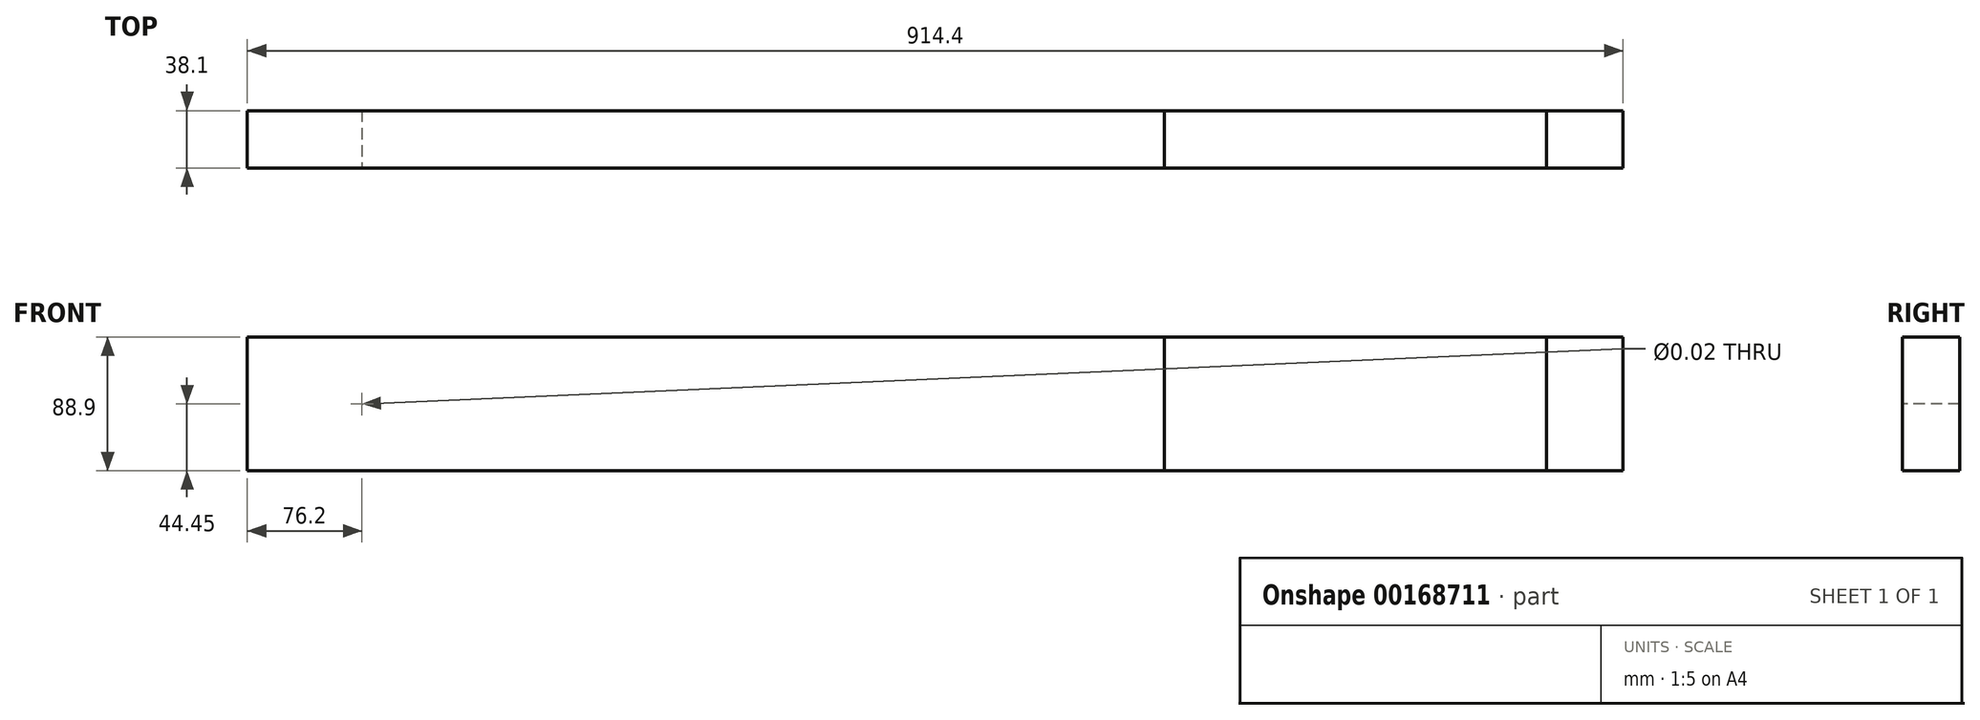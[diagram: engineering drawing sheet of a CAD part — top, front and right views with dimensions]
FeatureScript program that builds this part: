
annotation { "Feature Type Name" : "Feature", "Feature Type Description" : "" }
export const myFeature = defineFeature(function(context is Context, id is Id, definition is map)
    precondition{}
    {
        {
            var Q0;
            Q0=qCreatedBy(makeId("Right.planeOp"),FACE);
            var sketch = newSketch(context, id + "F0", { "sketchPlane" : qUnion([Q0])});
            skLineSegment(sketch, "E0.bottom", {"start": v(19.05, 44.45) * mm, "end": v(-19.05, 44.45) * mm});
            skLineSegment(sketch, "E0.top", {"start": v(19.05, -44.45) * mm, "end": v(-19.05, -44.45) * mm});
            skLineSegment(sketch, "E0.left", {"start": v(19.05, 44.45) * mm, "end": v(19.05, -44.45) * mm});
            skLineSegment(sketch, "E0.right", {"start": v(-19.05, 44.45) * mm, "end": v(-19.05, -44.45) * mm});
            skPoint(sketch, "E0.middle", {"position": v(0, 0) * mm});
            skSolve(sketch);
        }
        {
            var Q0;
            Q0=makeQuery(id+"F0.imprint","IMPRINT",FACE,{"disambiguationData":[TD([[makeQuery(id+"F0.imprint","IMPRINT",EDGE,{"derivedFrom":sQuery(id+"F0.wireOp",EDGE,"E0.bottom")}),1.0]])]});
            extrude(context, id + "F1", {"entities" : qUnion([Q0]), "depth" : 152.4 * mm});
        }
        {
            var Q0;
            Q0=makeQuery(id+"F1.opExtrude","SWEPT_FACE",FACE,{"disambiguationData":[OSD([sQuery(id+"F0.wireOp",EDGE,"E0.right")])]});
            var sketch = newSketch(context, id + "F2", { "sketchPlane" : qUnion([Q0])});
            skLineSegment(sketch, "E1", {"start": v(0, 0) * mm, "end": v(152.4, 0) * mm, "construction": true});
            skPoint(sketch, "E2", {"position": v(76.2, 0) * mm});
            skSolve(sketch);
        }
        {
            var Q0;
            Q0=sQuery(id+"F2.wireOp",VERTEX,"E2");
            var Q1;
            Q1=makeQuery(id+"F1.opExtrude","SWEPT_BODY",BODY,{"disambiguationData":[OSD([sQuery(id+"F0.wireOp",EDGE,"E0.bottom"),sQuery(id+"F0.wireOp",EDGE,"E0.top"),sQuery(id+"F0.wireOp",EDGE,"E0.left"),sQuery(id+"F0.wireOp",EDGE,"E0.right")])]});
            hole(context, id + "F3", {"style" : HoleStyle.SIMPLE, "endStyle" : HoleEndStyle.THROUGH, "standardTappedOrClearance" : lookupTablePath({ "standard" : "ANSI", "size" : "1/2 (0.5)", "type" : "Drilled" }), "standardBlindInLast" : lookupTablePath({ "standard" : "ANSI", "size" : "1/2", "type" : "Drilled" }), "holeDiameter" : 1 / 50.8 * mm, "locations" : qUnion([Q0]), "scope" : qUnion([Q1]), "isTappedThrough" : true});
        }
        {
            var Q0;
            Q0=makeQuery(id+"F1.opExtrude","CAP_FACE",FACE,{"disambiguationData":[OSD([sQuery(id+"F0.wireOp",EDGE,"E0.bottom"),sQuery(id+"F0.wireOp",EDGE,"E0.top"),sQuery(id+"F0.wireOp",EDGE,"E0.left"),sQuery(id+"F0.wireOp",EDGE,"E0.right")])],"isStart":false});
            extrude(context, id + "F4", {"entities" : qUnion([Q0]), "operationType" : NewBodyOperationType.ADD, "depth" : 711.2 * mm});
        }
        {
            var Q0;
            Q0=qSketchRegion(id+"F0",true);
            extrude(context, id + "F5", {"entities" : qUnion([Q0]), "depth" : 914.4 * mm});
        }
        {
            var Q0;
            Q0=qSketchRegion(id+"F0",true);
            extrude(context, id + "F6", {"entities" : qUnion([Q0]), "depth" : 609.6 * mm});
        }
    });
